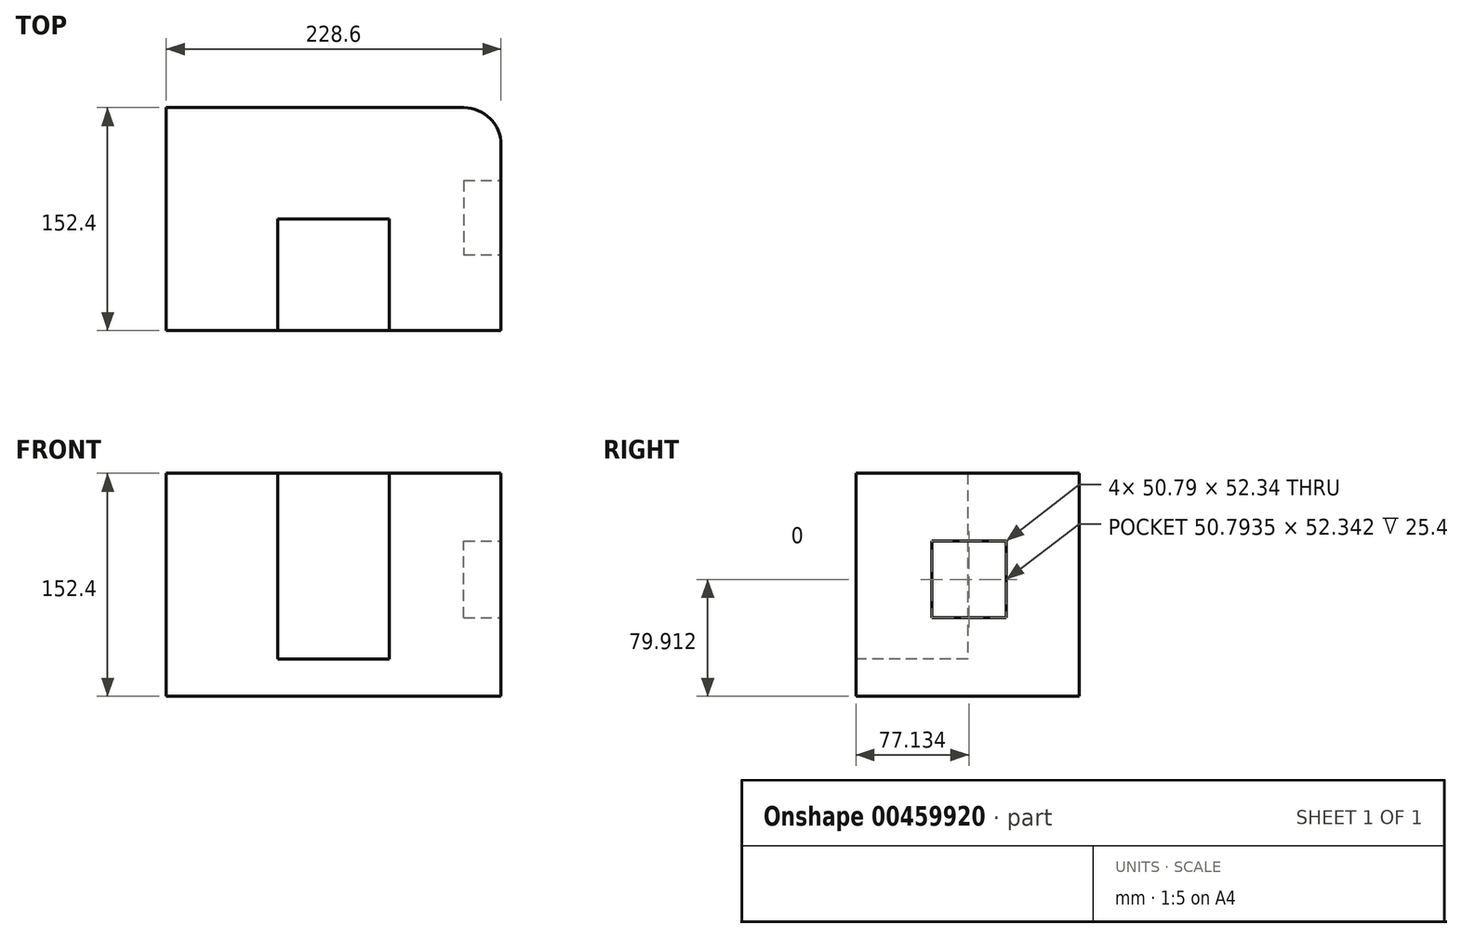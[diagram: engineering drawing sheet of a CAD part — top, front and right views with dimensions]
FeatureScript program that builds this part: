
annotation { "Feature Type Name" : "Feature", "Feature Type Description" : "" }
export const myFeature = defineFeature(function(context is Context, id is Id, definition is map)
    precondition{}
    {
        {
            var Q0;
            Q0=qCreatedBy(makeId("Front.planeOp"),FACE);
            var sketch = newSketch(context, id + "F0", { "sketchPlane" : qUnion([Q0])});
            skLineSegment(sketch, "E0", {"start": v(0, 0) * mm, "end": v(-228.6, 0) * mm});
            skLineSegment(sketch, "E1", {"start": v(-228.6, 0) * mm, "end": v(-228.6, 152.4) * mm});
            skLineSegment(sketch, "E2", {"start": v(-228.6, 152.4) * mm, "end": v(0, 152.4) * mm});
            skLineSegment(sketch, "E3", {"start": v(0, 152.4) * mm, "end": v(0, 0) * mm});
            skSolve(sketch);
        }
        {
            var Q0;
            Q0=makeQuery(id+"F0.imprint","IMPRINT",FACE,{"disambiguationData":[TD([[makeQuery(id+"F0.imprint","IMPRINT",EDGE,{"derivedFrom":sQuery(id+"F0.wireOp",EDGE,"E0")}),-1.0]])]});
            extrude(context, id + "F1", {"entities" : qUnion([Q0]), "depth" : 152.4 * mm});
        }
        {
            var Q0;
            Q0=makeQuery(id+"F1.opExtrude","CAP_FACE",FACE,{"disambiguationData":[OSD([sQuery(id+"F0.wireOp",EDGE,"E0"),sQuery(id+"F0.wireOp",EDGE,"E1"),sQuery(id+"F0.wireOp",EDGE,"E2"),sQuery(id+"F0.wireOp",EDGE,"E3")])],"isStart":false});
            var sketch = newSketch(context, id + "F2", { "sketchPlane" : qUnion([Q0])});
            skLineSegment(sketch, "E4", {"start": v(-228.6, 152.4) * mm, "end": v(-152.4, 152.4) * mm});
            skLineSegment(sketch, "E5", {"start": v(-152.4, 152.4) * mm, "end": v(-152.4, 25.4) * mm});
            skLineSegment(sketch, "E6", {"start": v(-152.4, 25.4) * mm, "end": v(-76.2, 25.4) * mm});
            skLineSegment(sketch, "E7", {"start": v(-76.2, 25.4) * mm, "end": v(-76.2, 152.4) * mm});
            skLineSegment(sketch, "E8", {"start": v(-76.2, 152.4) * mm, "end": v(0, 152.4) * mm});
            skSolve(sketch);
        }
        {
            var Q0;
            {var subQ0=sQuery(id+"F2.wireOp",EDGE,"E5");Q0=makeQuery(id+"F2.imprint","IMPRINT",FACE,{"disambiguationData":[TD([[makeQuery(id+"F2.imprint","IMPRINT",EDGE,{"derivedFrom":subQ0}),1.0]])]});}
            extrude(context, id + "F3", {"entities" : qUnion([Q0]), "operationType" : NewBodyOperationType.REMOVE, "oppositeDirection" : true, "depth" : 76.2 * mm});
        }
        {
            var Q0;
            Q0=makeQuery(id+"F1.opExtrude","SWEPT_FACE",FACE,{"disambiguationData":[OSD([sQuery(id+"F0.wireOp",EDGE,"E3")])]});
            var sketch = newSketch(context, id + "F4", { "sketchPlane" : qUnion([Q0])});
            skLineSegment(sketch, "E9", {"start": v(-152.4, 0) * mm, "end": v(-100.66, 0) * mm});
            skLineSegment(sketch, "E10", {"start": v(-100.66, 0) * mm, "end": v(-100.66, 106.08) * mm});
            skLineSegment(sketch, "E11", {"start": v(-100.66, 106.08) * mm, "end": v(-49.87, 106.08) * mm});
            skLineSegment(sketch, "E12", {"start": v(-49.87, 106.08) * mm, "end": v(-49.87, 53.74) * mm});
            skLineSegment(sketch, "E13", {"start": v(-49.87, 53.74) * mm, "end": v(-100.66, 53.74) * mm});
            skSolve(sketch);
        }
        {
            var Q0;
            {var subQ0=sQuery(id+"F4.wireOp",EDGE,"E11");Q0=makeQuery(id+"F4.imprint","IMPRINT",FACE,{"disambiguationData":[TD([[makeQuery(id+"F4.imprint","IMPRINT",EDGE,{"derivedFrom":subQ0}),-1.0]])]});}
            extrude(context, id + "F5", {"entities" : qUnion([Q0]), "operationType" : NewBodyOperationType.REMOVE, "oppositeDirection" : true, "depth" : 25.4 * mm});
        }
        {
            var Q0;
            Q0=makeQuery(id+"F1.opExtrude","CAP_EDGE",EDGE,{"disambiguationData":[OSD([sQuery(id+"F0.wireOp",EDGE,"E3")])],"isStart":true});
            fillet(context, id + "F6", {"entities" : qUnion([Q0]), "radius" : 25.4 * mm, "tangentPropagation" : true, "allowEdgeOverflow" : false});
        }
    });
